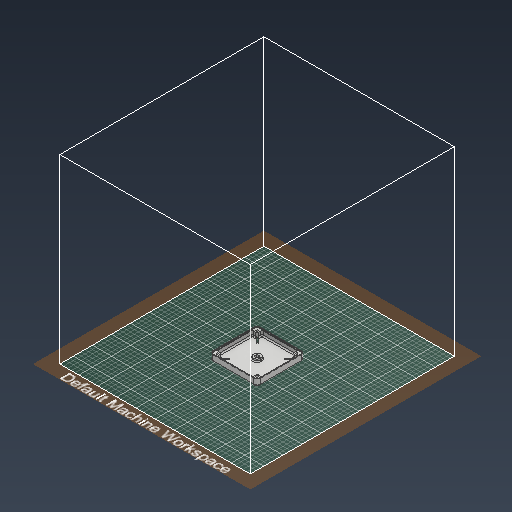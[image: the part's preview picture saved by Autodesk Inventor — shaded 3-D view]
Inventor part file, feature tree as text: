
AUTODESK INVENTOR PART (.ipt)
format: ipt  version: 2021 (Build 250183000, 183)  size: 756,736 bytes
history: native  units: mm
features: sketch x9, extrude x8, other x5, projected_geometry x4, fillet x3, reference x1
ambient origin geometry x8: Origin, YZ Plane, XZ Plane, XY Plane, X Axis, Y Axis, Z Axis, Center Point
bodies: Body1 (feature_tree)
feature tree (30):
  other  "Твердое тело1"
  extrude  "Выдавливание1"  Depth=2.5mm TaperAngle=0.0deg
  extrude  "Выдавливание2"  Depth=2.5mm
  other  "Выступ1"
  extrude  "Выдавливание3"  Depth=12.0mm TaperAngle=0.0deg
  fillet  "Сопряжение1"  Radius=6.0mm
  extrude  "Выдавливание4"  Depth=10.5mm
  fillet  "Сопряжение3"  Radius=6.0mm
  extrude  "Выдавливание5"  Depth=10.5mm
  sketch  "Эскиз6"
  extrude  "Выдавливание6"  Depth=6.0mm
  fillet  "Сопряжение4"  Radius=10.5mm
  extrude  "Выдавливание7"  Depth=10.0mm TaperAngle=0.0deg
  extrude  "Выдавливание8"  Depth=3.0mm
  sketch  "Эскиз1"
  sketch  "Эскиз2"
  projected_geometry  "Спроецированная петля1"
  sketch  "Эскиз3"
  projected_geometry  "Спроецированная петля2"
  sketch  "Эскиз4"
  sketch  "Эскиз5"
  reference  "Ссылка1"
  sketch  "Эскиз7"
  sketch  "Эскиз8"
  projected_geometry  "Спроецированная петля3"
  sketch  "Эскиз9"
  projected_geometry  "Спроецированная петля4"
  other  "<userpath>\Documents\GitHub\Tesla_coil_V1\3dModels\TeslaCoil.iam"
  other  "TeslaCoil.iam"
  other  "RackeSecondary:1"
